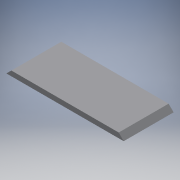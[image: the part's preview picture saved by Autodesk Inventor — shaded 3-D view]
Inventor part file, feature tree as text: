
AUTODESK INVENTOR PART (.ipt)
format: ipt  version: 2018.3 (Build 223284000, 284)  size: 271,872 bytes
history: native  units: mm
features: extrude x6, sketch x6, chamfer x2
ambient origin geometry x8: Origin, YZ Plane, XZ Plane, XY Plane, X Axis, Y Axis, Z Axis, Center Point
bodies: Solid1 (feature_tree)
feature tree (14):
  extrude  "Extrusion1"  Depth=20.0mm
  extrude  "Extrusion2"  Depth=2.0mm
  extrude  "Extrusion5"  Depth=20.0mm TaperAngle=0.0deg
  extrude  "Extrusion6"  Depth=10.0mm
  extrude  "Extrusion7"  Depth=5.0mm
  extrude  "Extrusion8"  Depth=1.5mm TaperAngle=0.0deg
  chamfer  "Chamfer1"  Distance=1.5mm
  chamfer  "Chamfer2"  Distance=0.5mm
  sketch  "Sketch1"  dims[d0=43.0mm d1=20.0mm]
  sketch  "Sketch2"  dims[d2=2.0mm d3=0.0mm d4=2.0mm]
  sketch  "Sketch5"  dims[d5=2.0mm d6=20.0mm d7=0.0mm]
  sketch  "Sketch6"  dims[d26=20.0mm d27=10.0mm]
  sketch  "Sketch7"  dims[d28=5.0mm d29=5.0mm]
  sketch  "Sketch8"  dims[d30=5.0mm d31=1.5mm d32=0.0mm d33=1.5mm d34=0.0mm d35=0.5mm d36=2.0mm d37=0.0mm d38=25.0mm d39=0.5mm d40=2.0mm d41=0.0mm d42=0.5mm d43=2.0mm d44=45.0deg d45=0.5mm d46=2.0mm d47=45.0deg]
